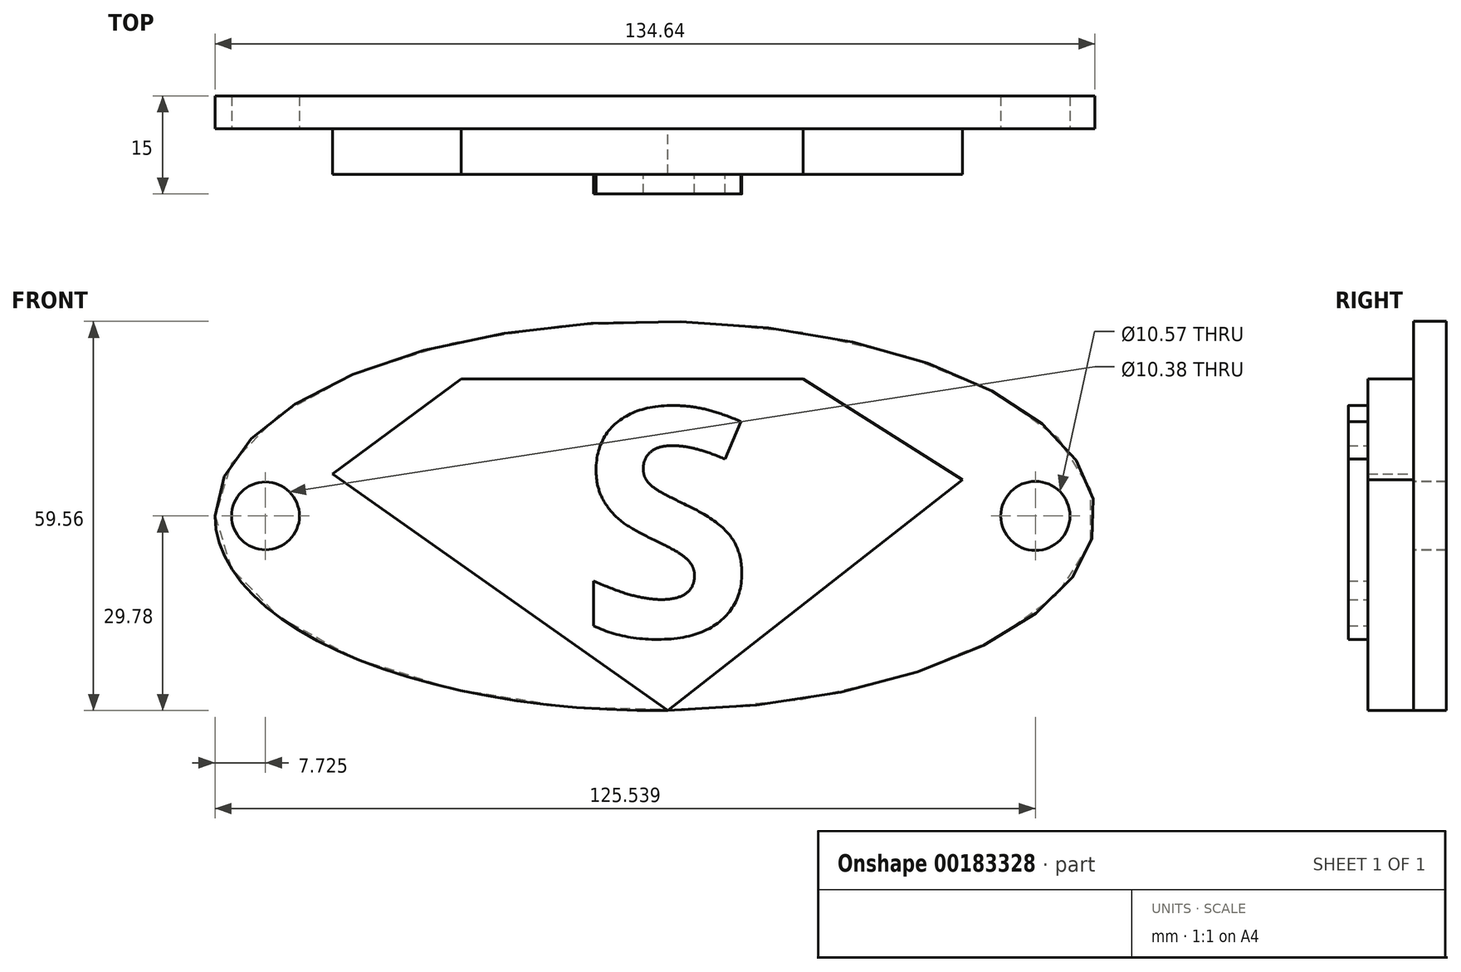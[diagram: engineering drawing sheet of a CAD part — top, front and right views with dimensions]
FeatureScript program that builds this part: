
annotation { "Feature Type Name" : "Feature", "Feature Type Description" : "" }
export const myFeature = defineFeature(function(context is Context, id is Id, definition is map)
    precondition{}
    {
        {
            var Q0;
            Q0=qCreatedBy(makeId("Front.planeOp"),FACE);
            var sketch = newSketch(context, id + "F0", { "sketchPlane" : qUnion([Q0])});
            skEllipse(sketch, "E0", {"center": v(0, 0) * mm, "majorRadius": 67.32 * mm, "minorRadius": 29.78 * mm, "majorAxis": v(-1, 0)});
            skSolve(sketch);
        }
        {
            var Q0;
            Q0 = qSketchRegion(id + "F0", true);
            extrude(context, id + "F1", {"entities" : qUnion([Q0]), "depth" : 5 * mm});
        }
        {
            var Q0;
            Q0=makeQuery(id+"F1.opExtrude","CAP_FACE",FACE,{"disambiguationData":[OSD([sQuery(id+"F0.wireOp",EDGE,"E0")])],"isStart":false});
            var sketch = newSketch(context, id + "F2", { "sketchPlane" : qUnion([Q0])});
            skLineSegment(sketch, "E1", {"start": v(22.66, 20.97) * mm, "end": v(-29.67, 20.97) * mm});
            skLineSegment(sketch, "E2", {"start": v(-29.67, 20.97) * mm, "end": v(-49.35, 6.42) * mm});
            skLineSegment(sketch, "E3", {"start": v(-49.35, 6.42) * mm, "end": v(1.97, -29.76) * mm});
            skLineSegment(sketch, "E4", {"start": v(1.97, -29.76) * mm, "end": v(47.06, 5.56) * mm});
            skLineSegment(sketch, "E5", {"start": v(47.06, 5.56) * mm, "end": v(22.66, 20.97) * mm});
            skSolve(sketch);
        }
        {
            var Q0;
            Q0 = qSketchRegion(id + "F2", true);
            extrude(context, id + "F3", {"entities" : qUnion([Q0]), "operationType" : NewBodyOperationType.ADD, "depth" : 7 * mm});
        }
        {
            var Q0;
            Q0=makeQuery(id+"F3.opExtrude","CAP_FACE",FACE,{"disambiguationData":[OSD([sQuery(id+"F2.wireOp",EDGE,"E1"),sQuery(id+"F2.wireOp",EDGE,"E2"),sQuery(id+"F2.wireOp",EDGE,"E3"),sQuery(id+"F2.wireOp",EDGE,"E4"),sQuery(id+"F2.wireOp",EDGE,"E5")])],"isStart":false});
            var sketch = newSketch(context, id + "F4", { "sketchPlane" : qUnion([Q0])});
            skText(sketch, "E6", { "text": "S", "fontName": "OpenSans-Bold.ttf"});
            const initialGuessF4  = {"E6": [-0.01165, -0.01842, 1, 0, 0.03512]};
            skSetInitialGuess(sketch, initialGuessF4);
            skSolve(sketch);
        }
        {
            var Q0;
            Q0=makeQuery(id+"F4.imprint","IMPRINT",FACE,{"disambiguationData":[TD([[makeQuery(id+"F4.imprint","IMPRINT",EDGE,{"derivedFrom":sQuery(id+"F4.wireOp",EDGE,"E6.sketch_text.stroke-0")}),-1.0]])]});
            extrude(context, id + "F5", {"entities" : qUnion([Q0]), "operationType" : NewBodyOperationType.ADD, "depth" : 3 * mm});
        }
        {
            var Q0;
            Q0=makeQuery(id+"F1.opExtrude","CAP_FACE",FACE,{"disambiguationData":[OSD([sQuery(id+"F0.wireOp",EDGE,"E0")])],"isStart":false});
            var sketch = newSketch(context, id + "F6", { "sketchPlane" : qUnion([Q0])});
            skCircle(sketch, "E7", {"center": v(-59.6, 0) * mm, "radius": 5.2 * mm});
            skCircle(sketch, "E8", {"center": v(58.22, 0) * mm, "radius": 5.28 * mm});
            skSolve(sketch);
        }
        {
            var Q0;
            Q0 = qSketchRegion(id + "F6", true);
            extrude(context, id + "F7", {"entities" : qUnion([Q0]), "operationType" : NewBodyOperationType.REMOVE, "oppositeDirection" : true, "depth" : 25 * mm});
        }
    });
